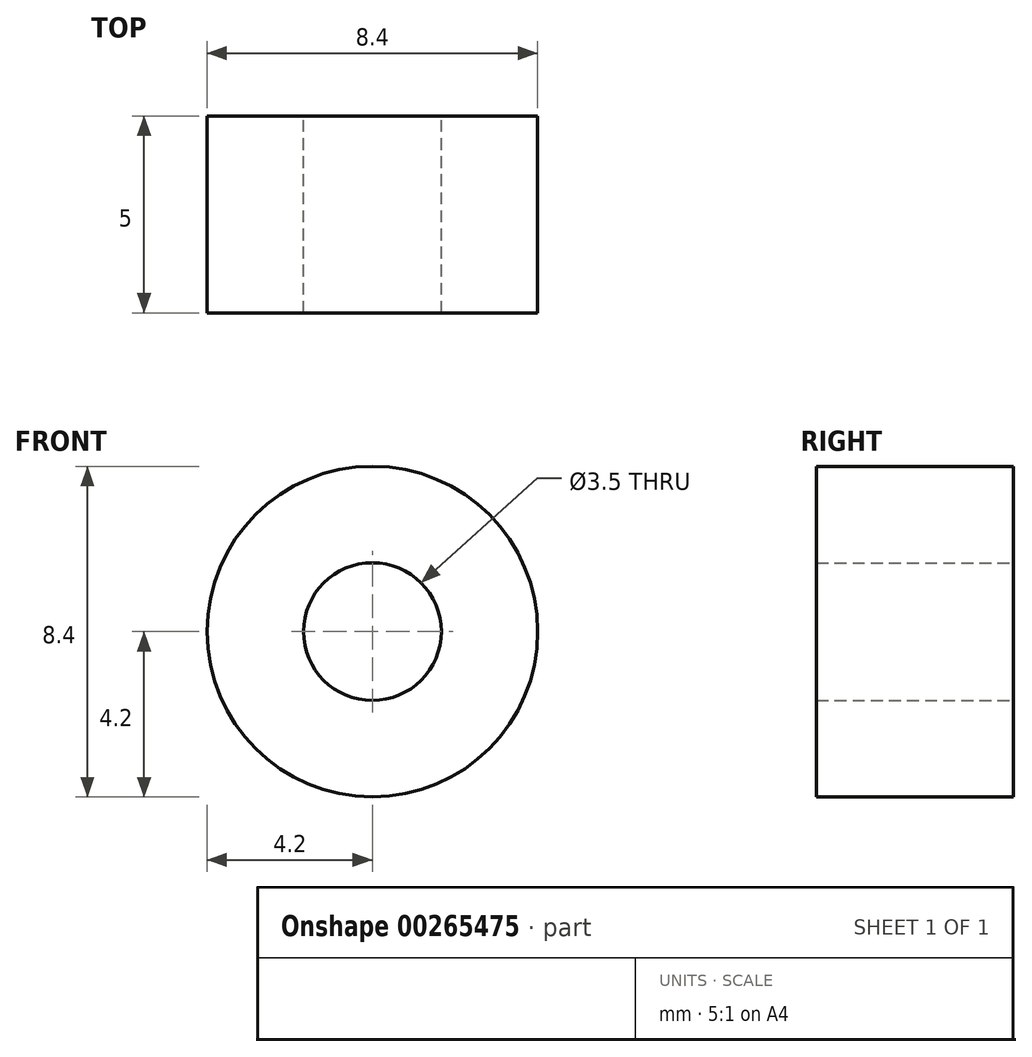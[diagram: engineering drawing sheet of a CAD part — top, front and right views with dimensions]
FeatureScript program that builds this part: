
annotation { "Feature Type Name" : "Feature", "Feature Type Description" : "" }
export const myFeature = defineFeature(function(context is Context, id is Id, definition is map)
    precondition{}
    {
        {
            var Q0;
            Q0=qCreatedBy(makeId("Front.planeOp"),FACE);
            var sketch = newSketch(context, id + "F0", { "sketchPlane" : qUnion([Q0])});
            skCircle(sketch, "E0", {"center": v(0, 0) * mm, "radius": 4.2 * mm});
            skCircle(sketch, "E1", {"center": v(0, 0) * mm, "radius": 1.75 * mm});
            skSolve(sketch);
        }
        {
            var Q0;
            Q0=makeQuery(id+"F0.imprint","IMPRINT",FACE,{"disambiguationData":[TD([[makeQuery(id+"F0.imprint","IMPRINT",EDGE,{"derivedFrom":sQuery(id+"F0.wireOp",EDGE,"E0")}),1.0]])]});
            extrude(context, id + "F1", {"entities" : qUnion([Q0]), "depth" : 5 * mm});
        }
    });
